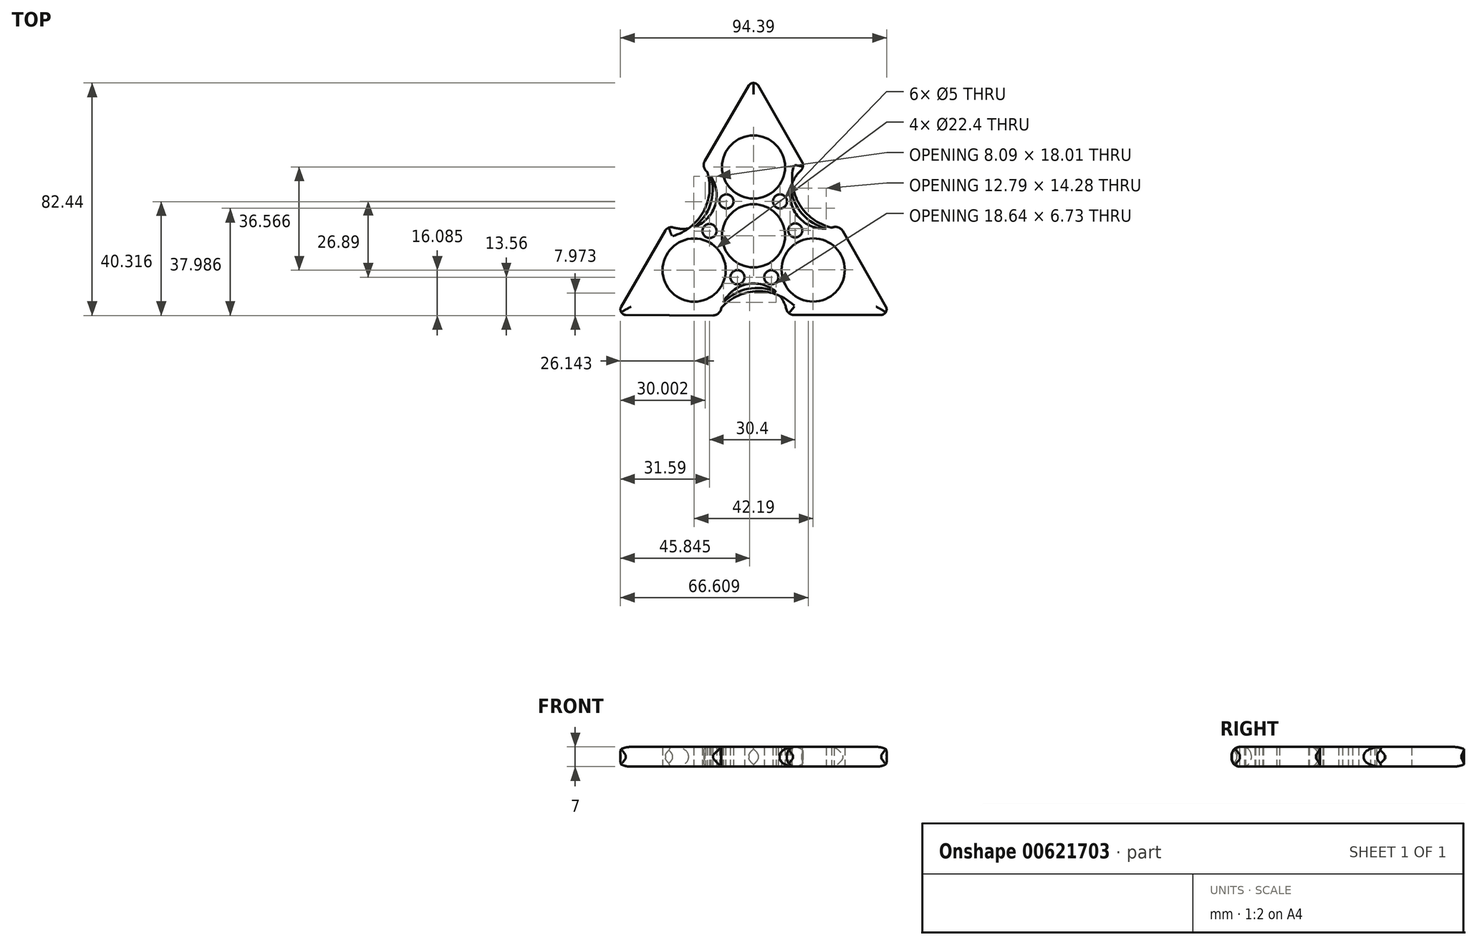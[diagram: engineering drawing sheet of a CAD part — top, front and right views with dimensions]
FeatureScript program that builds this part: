
annotation { "Feature Type Name" : "Feature", "Feature Type Description" : "" }
export const myFeature = defineFeature(function(context is Context, id is Id, definition is map)
    precondition{}
    {
        {
            var Q0;
            Q0=qCreatedBy(makeId("Top.planeOp"),FACE);
            var sketch = newSketch(context, id + "F0", { "sketchPlane" : qUnion([Q0])});
            skCircle(sketch, "E0", {"center": v(0, 0) * mm, "radius": 11.2 * mm});
            skCircle(sketch, "E1", {"center": v(0, 24.4) * mm, "radius": 11.2 * mm});
            skCircle(sketch, "E2.1.0", {"center": v(-21.05, -12.18) * mm, "radius": 11.2 * mm});
            skCircle(sketch, "E2.2.0", {"center": v(21.14, -12.12) * mm, "radius": 11.2 * mm});
            skPoint(sketch, "E2.center", {"position": v(0.03, 0.03) * mm});
            skLineSegment(sketch, "E3", {"start": v(-21.05, -12.18) * mm, "end": v(47.7, 27.39) * mm, "construction": true});
            skLineSegment(sketch, "E4", {"start": v(21.14, -12.12) * mm, "end": v(-50.9, 28.53) * mm, "construction": true});
            skLineSegment(sketch, "E5", {"start": v(0, 24.4) * mm, "end": v(0, -37.26) * mm, "construction": true});
            skLineSegment(sketch, "E6", {"start": v(-21.05, -12.18) * mm, "end": v(26.7, 58.1) * mm, "construction": true});
            skLineSegment(sketch, "E7", {"start": v(21.14, -12.12) * mm, "end": v(-19.53, 58.56) * mm, "construction": true});
            skLineSegment(sketch, "E8", {"start": v(0, 24.4) * mm, "end": v(41.86, 24.4) * mm, "construction": true});
            skLineSegment(sketch, "E9", {"start": v(0, 24.4) * mm, "end": v(-48.44, 24.4) * mm, "construction": true});
            skLineSegment(sketch, "E10", {"start": v(-21.05, -12.18) * mm, "end": v(21.14, -12.12) * mm, "construction": true});
            skLineSegment(sketch, "E11", {"start": v(0, 24.4) * mm, "end": v(0, 70.93) * mm, "construction": true});
            skLineSegment(sketch, "E12", {"start": v(-18.56, 24.4) * mm, "end": v(0, 56.19) * mm});
            skLineSegment(sketch, "E13", {"start": v(0, 56.19) * mm, "end": v(18.3, 24.4) * mm});
            skLineSegment(sketch, "E14", {"start": v(-21.05, -12.18) * mm, "end": v(-58.65, -33.82) * mm, "construction": true});
            skLineSegment(sketch, "E15", {"start": v(21.14, -12.12) * mm, "end": v(60.21, -34.16) * mm, "construction": true});
            skLineSegment(sketch, "E16", {"start": v(-21.05, -12.18) * mm, "end": v(-66.53, -12.18) * mm, "construction": true});
            skLineSegment(sketch, "E17", {"start": v(-21.05, -12.18) * mm, "end": v(-43.33, -44.98) * mm, "construction": true});
            skLineSegment(sketch, "E18", {"start": v(21.14, -12.12) * mm, "end": v(66.5, -12.12) * mm, "construction": true});
            skLineSegment(sketch, "E19", {"start": v(21.14, -12.12) * mm, "end": v(41.4, -47.31) * mm, "construction": true});
            skLineSegment(sketch, "E20.1.0", {"start": v(-48.66, -28.1) * mm, "end": v(-30.27, 3.65) * mm});
            skLineSegment(sketch, "E20.1.1", {"start": v(-11.84, -28.27) * mm, "end": v(-48.66, -28.1) * mm});
            skLineSegment(sketch, "E20.2.0", {"start": v(48.66, -28.1) * mm, "end": v(11.97, -28.04) * mm});
            skLineSegment(sketch, "E20.2.1", {"start": v(30.4, 3.88) * mm, "end": v(48.66, -28.1) * mm});
            skArc(sketch, "E21", {"start": v(-30.27, 3.65) * mm, "mid": v(-14.63, 8.5) * mm, "end": v(-18.56, 24.4) * mm});
            skArc(sketch, "E22.1.0", {"start": v(11.97, -28.04) * mm, "mid": v(-0.04, -16.92) * mm, "end": v(-11.84, -28.27) * mm});
            skArc(sketch, "E22.2.0", {"start": v(18.3, 24.4) * mm, "mid": v(14.67, 8.42) * mm, "end": v(30.4, 3.88) * mm});
            skArc(sketch, "E23", {"start": v(44.93, -28.09) * mm, "mid": v(46.93, -27.08) * mm, "end": v(46.8, -24.84) * mm});
            skArc(sketch, "E24.1.0", {"start": v(1.86, 52.95) * mm, "mid": v(-0.02, 54.18) * mm, "end": v(-1.9, 52.95) * mm});
            skArc(sketch, "E24.2.0", {"start": v(-46.79, -24.86) * mm, "mid": v(-46.91, -27.1) * mm, "end": v(-44.9, -28.11) * mm});
            skArc(sketch, "E25", {"start": v(11.52, -25.48) * mm, "mid": v(12.5, -27.42) * mm, "end": v(14.58, -28.05) * mm});
            skArc(sketch, "E26.1.0", {"start": v(16.3, 22.71) * mm, "mid": v(17.5, 24.53) * mm, "end": v(17, 26.65) * mm});
            skArc(sketch, "E26.2.0", {"start": v(-27.82, 2.77) * mm, "mid": v(-30, 2.9) * mm, "end": v(-31.58, 1.4) * mm});
            skArc(sketch, "E27", {"start": v(-14.3, -28.26) * mm, "mid": v(-12.32, -27.4) * mm, "end": v(-11.37, -25.48) * mm});
            skArc(sketch, "E28.1.0", {"start": v(31.62, 1.75) * mm, "mid": v(29.9, 3.03) * mm, "end": v(27.75, 2.9) * mm});
            skArc(sketch, "E28.2.0", {"start": v(-17.32, 26.51) * mm, "mid": v(-17.58, 24.38) * mm, "end": v(-16.38, 22.59) * mm});
            skCircle(sketch, "E29", {"center": v(-9.61, 12.19) * mm, "radius": 2.5 * mm});
            skCircle(sketch, "E30.1.0.0", {"center": v(9.39, 12.19) * mm, "radius": 2.5 * mm});
            skLineSegment(sketch, "E30.direction1", {"start": v(-9.61, 12.19) * mm, "end": v(9.39, 12.19) * mm, "construction": true});
            skCircle(sketch, "E31.1.0.0", {"center": v(14.8, 1.9) * mm, "radius": 2.5 * mm});
            skLineSegment(sketch, "E31.direction1", {"start": v(9.39, 12.19) * mm, "end": v(14.8, 1.9) * mm, "construction": true});
            skCircle(sketch, "E32.1.0.0", {"center": v(6.3, -14.7) * mm, "radius": 2.5 * mm});
            skLineSegment(sketch, "E32.direction1", {"start": v(14.8, 1.9) * mm, "end": v(6.3, -14.7) * mm, "construction": true});
            skCircle(sketch, "E33.1.0.0", {"center": v(-5.7, -14.7) * mm, "radius": 2.5 * mm});
            skLineSegment(sketch, "E33.direction1", {"start": v(6.3, -14.7) * mm, "end": v(-5.7, -14.7) * mm, "construction": true});
            skCircle(sketch, "E34.1.0.0", {"center": v(-15.6, 1.7) * mm, "radius": 2.5 * mm});
            skLineSegment(sketch, "E34.direction1", {"start": v(-5.7, -14.7) * mm, "end": v(-15.6, 1.7) * mm, "construction": true});
            skArc(sketch, "E35", {"start": v(-21.23, 3.05) * mm, "mid": v(-15.32, 11.09) * mm, "end": v(-15.15, 21.06) * mm});
            skArc(sketch, "E36", {"start": v(-23.08, 2.6) * mm, "mid": v(-16.5, 11.5) * mm, "end": v(-16.38, 22.59) * mm});
            skArc(sketch, "E37.1.0", {"start": v(7.98, -19.91) * mm, "mid": v(-1.94, -18.81) * mm, "end": v(-10.67, -23.65) * mm});
            skArc(sketch, "E37.1.1", {"start": v(9.3, -21.29) * mm, "mid": v(-1.71, -20.04) * mm, "end": v(-11.37, -25.48) * mm});
            skArc(sketch, "E37.2.0", {"start": v(13.26, 16.86) * mm, "mid": v(17.26, 7.73) * mm, "end": v(25.81, 2.59) * mm});
            skArc(sketch, "E37.2.1", {"start": v(13.78, 18.7) * mm, "mid": v(18.21, 8.54) * mm, "end": v(27.75, 2.9) * mm});
            skSolve(sketch);
        }
        {
            var Q0;
            {var subQ0=sQuery(id+"F0.wireOp",EDGE,"E35");Q0=makeQuery(id+"F0.imprint","IMPRINT",FACE,{"disambiguationData":[TD([[makeQuery(id+"F0.imprint","IMPRINT",EDGE,{"derivedFrom":subQ0}),1.0]])]});}
            var Q1;
            {var subQ0=sQuery(id+"F0.wireOp",EDGE,"E37.2.0");Q1=makeQuery(id+"F0.imprint","IMPRINT",FACE,{"disambiguationData":[TD([[makeQuery(id+"F0.imprint","IMPRINT",EDGE,{"derivedFrom":subQ0}),1.0]])]});}
            var Q2;
            {var subQ0=sQuery(id+"F0.wireOp",EDGE,"E37.1.0");Q2=makeQuery(id+"F0.imprint","IMPRINT",FACE,{"disambiguationData":[TD([[makeQuery(id+"F0.imprint","IMPRINT",EDGE,{"derivedFrom":subQ0}),1.0]])]});}
            var Q3;
            Q3=makeQuery(id+"F0.imprint","IMPRINT",FACE,{"disambiguationData":[TD([[makeQuery(id+"F0.imprint","IMPRINT",EDGE,{"derivedFrom":sQuery(id+"F0.wireOp",EDGE,"E0")}),-1.0]])]});
            extrude(context, id + "F1", {"entities" : qUnion([Q0, Q1, Q2, Q3]), "depth" : 7 * mm, "offsetDistance" : 25 * mm});
        }
        {
            var Q0;
            Q0=makeQuery(id+"F1.opExtrude","CAP_EDGE",EDGE,{"disambiguationData":[OSD([sQuery(id+"F0.wireOp",EDGE,"E20.1.0")])],"isStart":false});
            var Q1;
            Q1=makeQuery(id+"F1.opExtrude","CAP_EDGE",EDGE,{"disambiguationData":[OSD([sQuery(id+"F0.wireOp",EDGE,"E20.1.0")])],"isStart":true});
            var Q2;
            Q2=makeQuery(id+"F1.opExtrude","CAP_EDGE",EDGE,{"disambiguationData":[OSD([sQuery(id+"F0.wireOp",EDGE,"E12")])],"isStart":true});
            var Q3;
            Q3=makeQuery(id+"F1.opExtrude","CAP_EDGE",EDGE,{"disambiguationData":[OSD([sQuery(id+"F0.wireOp",EDGE,"E12")])],"isStart":false});
            var Q4;
            Q4=makeQuery(id+"F1.opExtrude","CAP_EDGE",EDGE,{"disambiguationData":[OSD([sQuery(id+"F0.wireOp",EDGE,"E13")])],"isStart":true});
            var Q5;
            Q5=makeQuery(id+"F1.opExtrude","CAP_EDGE",EDGE,{"disambiguationData":[OSD([sQuery(id+"F0.wireOp",EDGE,"E13")])],"isStart":false});
            var Q6;
            Q6=makeQuery(id+"F1.opExtrude","CAP_EDGE",EDGE,{"disambiguationData":[OSD([sQuery(id+"F0.wireOp",EDGE,"E20.2.1")])],"isStart":true});
            var Q7;
            Q7=makeQuery(id+"F1.opExtrude","CAP_EDGE",EDGE,{"disambiguationData":[OSD([sQuery(id+"F0.wireOp",EDGE,"E20.2.1")])],"isStart":false});
            var Q8;
            Q8=makeQuery(id+"F1.opExtrude","CAP_EDGE",EDGE,{"disambiguationData":[OSD([sQuery(id+"F0.wireOp",EDGE,"E20.2.0")])],"isStart":true});
            var Q9;
            Q9=makeQuery(id+"F1.opExtrude","CAP_EDGE",EDGE,{"disambiguationData":[OSD([sQuery(id+"F0.wireOp",EDGE,"E20.2.0")])],"isStart":false});
            var Q10;
            Q10=makeQuery(id+"F1.opExtrude","CAP_EDGE",EDGE,{"disambiguationData":[OSD([sQuery(id+"F0.wireOp",EDGE,"E20.1.1")])],"isStart":true});
            var Q11;
            Q11=makeQuery(id+"F1.opExtrude","CAP_EDGE",EDGE,{"disambiguationData":[OSD([sQuery(id+"F0.wireOp",EDGE,"E20.1.1")])],"isStart":false});
            var Q12;
            {var subQ0=sQuery(id+"F0.wireOp",EDGE,"E26.1.0");var subQ1=sQuery(id+"F0.wireOp",EDGE,"E22.2.0");var subQ2=makeQuery(id+"F0.imprint","INTERSECT",VERTEX,{"disambiguationData":[OD(0.0)],"derivedFrom":[subQ1,subQ0]});Q12=makeQuery(id+"F1.opExtrude","CAP_EDGE",EDGE,{"disambiguationData":[OSD([subQ1]),TDD([makeQuery(id+"F0.imprint","IMPRINT",EDGE,{"disambiguationData":[TD([[subQ2,1.0]])],"derivedFrom":subQ1}),makeQuery(id+"F0.imprint","IMPRINT",EDGE,{"disambiguationData":[TD([[subQ2,-1.0]])],"derivedFrom":subQ1})])],"isStart":true});}
            var Q13;
            {var subQ0=sQuery(id+"F0.wireOp",EDGE,"E26.1.0");var subQ1=sQuery(id+"F0.wireOp",EDGE,"E22.2.0");var subQ2=makeQuery(id+"F0.imprint","INTERSECT",VERTEX,{"disambiguationData":[OD(0.0)],"derivedFrom":[subQ1,subQ0]});Q13=makeQuery(id+"F1.opExtrude","CAP_EDGE",EDGE,{"disambiguationData":[OSD([subQ1]),TDD([makeQuery(id+"F0.imprint","IMPRINT",EDGE,{"disambiguationData":[TD([[subQ2,1.0]])],"derivedFrom":subQ1}),makeQuery(id+"F0.imprint","IMPRINT",EDGE,{"disambiguationData":[TD([[subQ2,-1.0]])],"derivedFrom":subQ1})])],"isStart":false});}
            var Q14;
            {var subQ0=sQuery(id+"F0.wireOp",EDGE,"E25");var subQ1=sQuery(id+"F0.wireOp",EDGE,"E22.1.0");var subQ2=makeQuery(id+"F0.imprint","INTERSECT",VERTEX,{"disambiguationData":[OD(0.0)],"derivedFrom":[subQ1,subQ0]});Q14=makeQuery(id+"F1.opExtrude","CAP_EDGE",EDGE,{"disambiguationData":[OSD([subQ1]),TDD([makeQuery(id+"F0.imprint","IMPRINT",EDGE,{"disambiguationData":[TD([[subQ2,1.0]])],"derivedFrom":subQ1}),makeQuery(id+"F0.imprint","IMPRINT",EDGE,{"disambiguationData":[TD([[subQ2,-1.0]])],"derivedFrom":subQ1})])],"isStart":true});}
            var Q15;
            {var subQ0=sQuery(id+"F0.wireOp",EDGE,"E25");var subQ1=sQuery(id+"F0.wireOp",EDGE,"E22.1.0");var subQ2=makeQuery(id+"F0.imprint","INTERSECT",VERTEX,{"disambiguationData":[OD(0.0)],"derivedFrom":[subQ1,subQ0]});Q15=makeQuery(id+"F1.opExtrude","CAP_EDGE",EDGE,{"disambiguationData":[OSD([subQ1]),TDD([makeQuery(id+"F0.imprint","IMPRINT",EDGE,{"disambiguationData":[TD([[subQ2,1.0]])],"derivedFrom":subQ1}),makeQuery(id+"F0.imprint","IMPRINT",EDGE,{"disambiguationData":[TD([[subQ2,-1.0]])],"derivedFrom":subQ1})])],"isStart":false});}
            var Q16;
            {var subQ0=sQuery(id+"F0.wireOp",EDGE,"E26.2.0");var subQ1=sQuery(id+"F0.wireOp",EDGE,"E21");var subQ2=makeQuery(id+"F0.imprint","INTERSECT",VERTEX,{"disambiguationData":[OD(0.0)],"derivedFrom":[subQ1,subQ0]});Q16=makeQuery(id+"F1.opExtrude","CAP_EDGE",EDGE,{"disambiguationData":[OSD([subQ1]),TDD([makeQuery(id+"F0.imprint","IMPRINT",EDGE,{"disambiguationData":[TD([[subQ2,1.0]])],"derivedFrom":subQ1}),makeQuery(id+"F0.imprint","IMPRINT",EDGE,{"disambiguationData":[TD([[subQ2,-1.0]])],"derivedFrom":subQ1})])],"isStart":false});}
            var Q17;
            {var subQ0=sQuery(id+"F0.wireOp",EDGE,"E26.2.0");var subQ1=sQuery(id+"F0.wireOp",EDGE,"E21");var subQ2=makeQuery(id+"F0.imprint","INTERSECT",VERTEX,{"disambiguationData":[OD(0.0)],"derivedFrom":[subQ1,subQ0]});Q17=makeQuery(id+"F1.opExtrude","CAP_EDGE",EDGE,{"disambiguationData":[OSD([subQ1]),TDD([makeQuery(id+"F0.imprint","IMPRINT",EDGE,{"disambiguationData":[TD([[subQ2,1.0]])],"derivedFrom":subQ1}),makeQuery(id+"F0.imprint","IMPRINT",EDGE,{"disambiguationData":[TD([[subQ2,-1.0]])],"derivedFrom":subQ1})])],"isStart":true});}
            fillet(context, id + "F2", {"entities" : qUnion([Q0, Q1, Q2, Q3, Q4, Q5, Q6, Q7, Q8, Q9, Q10, Q11, Q12, Q13, Q14, Q15, Q16, Q17]), "radius" : 3 * mm, "tangentPropagation" : true, "allowEdgeOverflow" : false});
        }
    });
